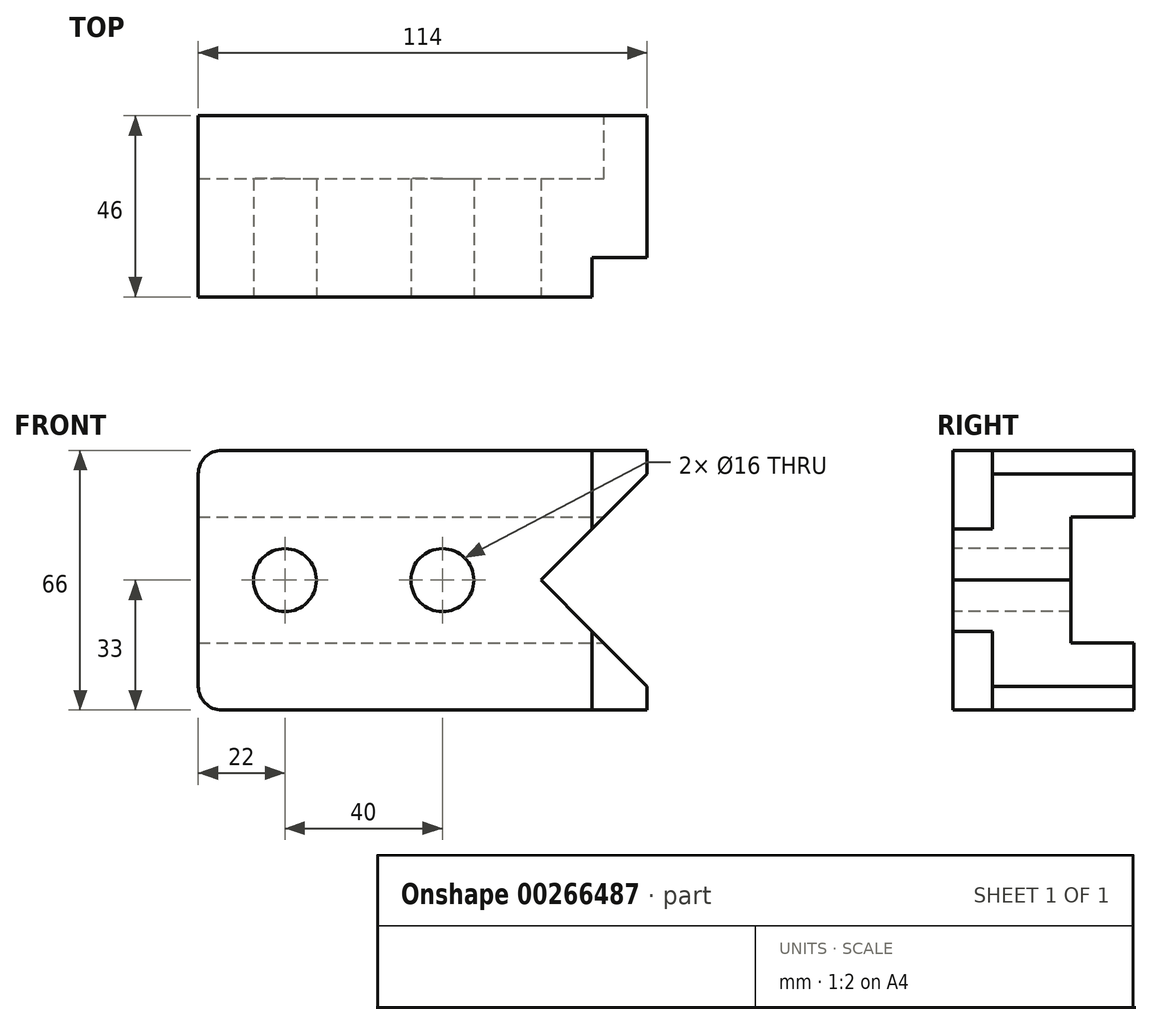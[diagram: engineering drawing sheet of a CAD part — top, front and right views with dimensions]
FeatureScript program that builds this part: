
annotation { "Feature Type Name" : "Feature", "Feature Type Description" : "" }
export const myFeature = defineFeature(function(context is Context, id is Id, definition is map)
    precondition{}
    {
        {
            var Q0;
            Q0=qCreatedBy(makeId("Top.planeOp"),FACE);
            var sketch = newSketch(context, id + "F0", { "sketchPlane" : qUnion([Q0])});
            skLineSegment(sketch, "E0.bottom", {"start": v(0, 0) * mm, "end": v(114, 0) * mm});
            skLineSegment(sketch, "E0.top", {"start": v(0, 46) * mm, "end": v(114, 46) * mm});
            skLineSegment(sketch, "E0.left", {"start": v(0, 0) * mm, "end": v(0, 46) * mm});
            skLineSegment(sketch, "E0.right", {"start": v(114, 0) * mm, "end": v(114, 46) * mm});
            skSolve(sketch);
        }
        {
            var Q0;
            Q0 = qSketchRegion(id + "F0", true);
            extrude(context, id + "F1", {"entities" : qUnion([Q0]), "endBound" : BoundingType.SYMMETRIC, "depth" : 66 * mm});
        }
        {
            var Q0;
            Q0=makeQuery(id+"F1.opExtrude","SWEPT_FACE",FACE,{"disambiguationData":[OSD([sQuery(id+"F0.wireOp",EDGE,"E0.bottom")])]});
            var sketch = newSketch(context, id + "F2", { "sketchPlane" : qUnion([Q0])});
            skLineSegment(sketch, "E1", {"start": v(114, 27) * mm, "end": v(87, 0) * mm});
            skLineSegment(sketch, "E2", {"start": v(87, 0) * mm, "end": v(114, -27) * mm});
            skLineSegment(sketch, "E3", {"start": v(0, 0) * mm, "end": v(114, 0) * mm, "construction": true});
            skCircle(sketch, "E4", {"center": v(22, 0) * mm, "radius": 8 * mm});
            skCircle(sketch, "E5", {"center": v(62, 0) * mm, "radius": 8 * mm});
            skSolve(sketch);
        }
        {
            var Q0;
            Q0=makeQuery(id+"F1.opExtrude","CAP_EDGE",EDGE,{"disambiguationData":[OSD([sQuery(id+"F0.wireOp",EDGE,"E0.left")])],"isStart":false});
            var Q1;
            Q1=makeQuery(id+"F1.opExtrude","CAP_EDGE",EDGE,{"disambiguationData":[OSD([sQuery(id+"F0.wireOp",EDGE,"E0.left")])],"isStart":true});
            fillet(context, id + "F3", {"entities" : qUnion([Q0, Q1]), "radius" : 6 * mm, "tangentPropagation" : true, "allowEdgeOverflow" : false});
        }
        {
            var Q0;
            {var subQ0=sQuery(id+"F2.wireOp",EDGE,"E1");Q0=makeQuery(id+"F2.imprint","IMPRINT",FACE,{"disambiguationData":[TD([[makeQuery(id+"F2.imprint","IMPRINT",EDGE,{"derivedFrom":subQ0}),1.0]])]});}
            var Q1;
            Q1=makeQuery(id+"F2.imprint","IMPRINT",FACE,{"disambiguationData":[TD([[makeQuery(id+"F2.imprint","IMPRINT",EDGE,{"derivedFrom":sQuery(id+"F2.wireOp",EDGE,"E4")}),1.0]])]});
            var Q2;
            Q2=makeQuery(id+"F2.imprint","IMPRINT",FACE,{"disambiguationData":[TD([[makeQuery(id+"F2.imprint","IMPRINT",EDGE,{"derivedFrom":sQuery(id+"F2.wireOp",EDGE,"E5")}),1.0]])]});
            extrude(context, id + "F4", {"entities" : qUnion([Q0, Q1, Q2]), "operationType" : NewBodyOperationType.REMOVE, "endBound" : BoundingType.THROUGH_ALL, "oppositeDirection" : true, "depth" : 25 * mm});
        }
        {
            var Q0;
            Q0=makeQuery(id+"F1.opExtrude","CAP_FACE",FACE,{"disambiguationData":[OSD([sQuery(id+"F0.wireOp",EDGE,"E0.bottom"),sQuery(id+"F0.wireOp",EDGE,"E0.top"),sQuery(id+"F0.wireOp",EDGE,"E0.left"),sQuery(id+"F0.wireOp",EDGE,"E0.right")])],"isStart":false});
            var sketch = newSketch(context, id + "F5", { "sketchPlane" : qUnion([Q0])});
            skLineSegment(sketch, "E6.bottom", {"start": v(114, 0) * mm, "end": v(100, 0) * mm});
            skLineSegment(sketch, "E6.top", {"start": v(114, 10) * mm, "end": v(100, 10) * mm});
            skLineSegment(sketch, "E6.left", {"start": v(114, 0) * mm, "end": v(114, 10) * mm});
            skLineSegment(sketch, "E6.right", {"start": v(100, 0) * mm, "end": v(100, 10) * mm});
            skSolve(sketch);
        }
        {
            var Q0;
            Q0 = qSketchRegion(id + "F5", true);
            extrude(context, id + "F6", {"entities" : qUnion([Q0]), "operationType" : NewBodyOperationType.REMOVE, "endBound" : BoundingType.THROUGH_ALL, "oppositeDirection" : true, "depth" : 25 * mm});
        }
        {
            var Q0;
            Q0=makeQuery(id+"F1.opExtrude","SWEPT_FACE",FACE,{"disambiguationData":[OSD([sQuery(id+"F0.wireOp",EDGE,"E0.top")])]});
            var sketch = newSketch(context, id + "F7", { "sketchPlane" : qUnion([Q0])});
            skLineSegment(sketch, "E7.bottom", {"start": v(0, 16) * mm, "end": v(-114, 16) * mm});
            skLineSegment(sketch, "E7.top", {"start": v(0, -16) * mm, "end": v(-114, -16) * mm});
            skLineSegment(sketch, "E7.left", {"start": v(0, 16) * mm, "end": v(0, -16) * mm});
            skLineSegment(sketch, "E7.right", {"start": v(-114, 16) * mm, "end": v(-114, -16) * mm});
            skPoint(sketch, "E8", {"position": v(0, 0) * mm});
            skSolve(sketch);
        }
        {
            var Q0;
            Q0 = qSketchRegion(id + "F7", true);
            extrude(context, id + "F8", {"entities" : qUnion([Q0]), "operationType" : NewBodyOperationType.REMOVE, "oppositeDirection" : true, "depth" : 16 * mm});
        }
    });
